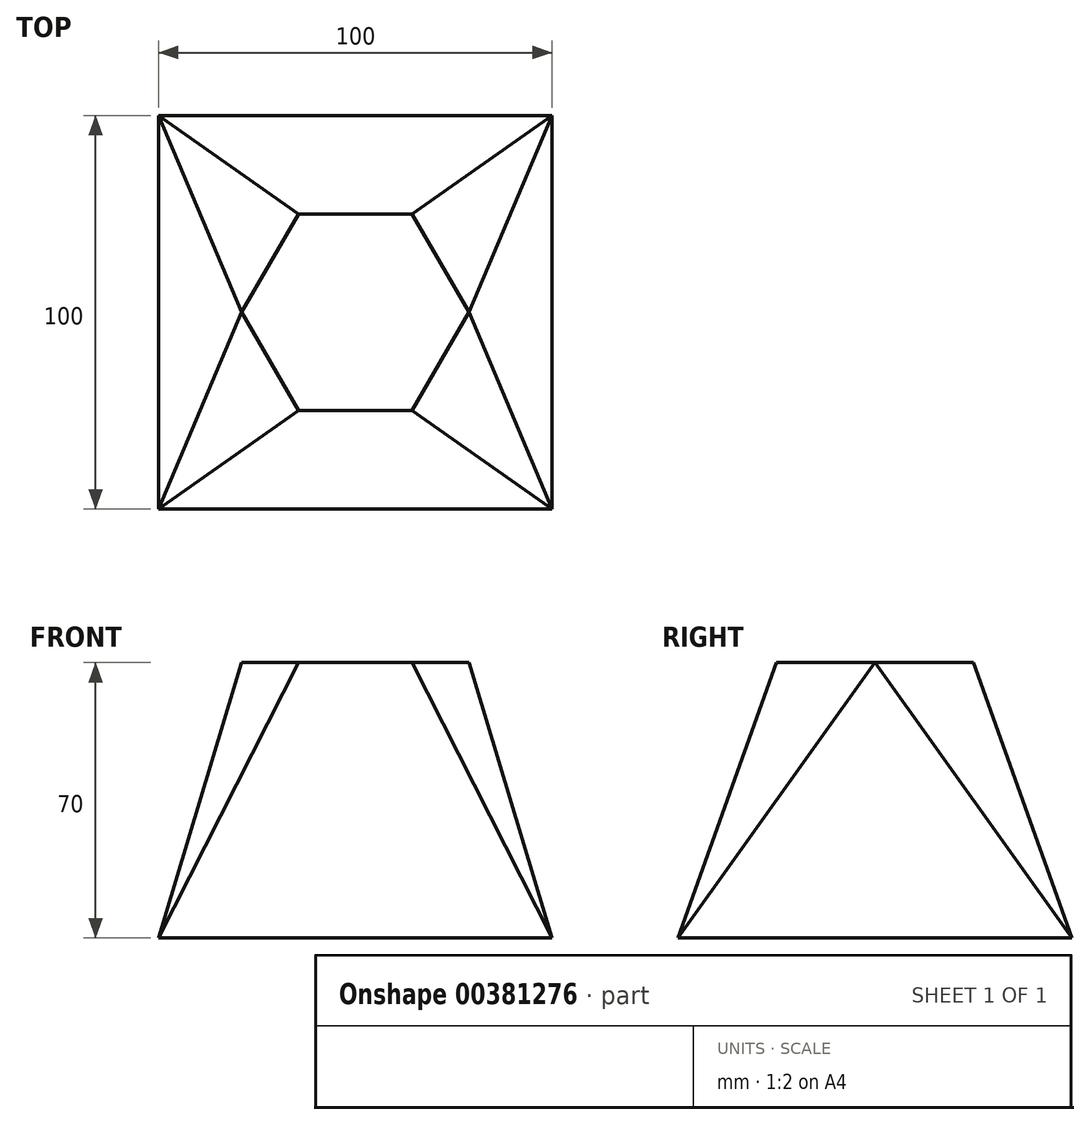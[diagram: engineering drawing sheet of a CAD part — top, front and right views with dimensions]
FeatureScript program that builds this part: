
annotation { "Feature Type Name" : "Feature", "Feature Type Description" : "" }
export const myFeature = defineFeature(function(context is Context, id is Id, definition is map)
    precondition{}
    {
        {
            var Q0;
            Q0=qCreatedBy(makeId("Top.planeOp"),FACE);
            var sketch = newSketch(context, id + "F0", { "sketchPlane" : qUnion([Q0])});
            skLineSegment(sketch, "E0.bottom", {"start": v(50, 50) * mm, "end": v(-50, 50) * mm});
            skLineSegment(sketch, "E0.top", {"start": v(50, -50) * mm, "end": v(-50, -50) * mm});
            skLineSegment(sketch, "E0.left", {"start": v(50, 50) * mm, "end": v(50, -50) * mm});
            skLineSegment(sketch, "E0.right", {"start": v(-50, 50) * mm, "end": v(-50, -50) * mm});
            skPoint(sketch, "E0.middle", {"position": v(0, 0) * mm});
            skSolve(sketch);
        }
        {
            var Q0;
            Q0=qCreatedBy(makeId("Top.planeOp"),FACE);
            cPlane(context, id + "F1", {"entities" : qUnion([Q0]), "cplaneType" : CPlaneType.OFFSET, "offset" : 70 * mm, "width" : 150 * mm, "height" : 150 * mm});
        }
        {
            var Q0;
            Q0=qCreatedBy(id+"F1.planeOp",FACE);
            var sketch = newSketch(context, id + "F2", { "sketchPlane" : qUnion([Q0])});
            skCircle(sketch, "E1.cCircle", {"center": v(0, 0) * mm, "radius": 25 * mm, "construction": true});
            skLineSegment(sketch, "E1.0", {"start": v(-14.43, 25) * mm, "end": v(14.43, 25) * mm});
            skLineSegment(sketch, "E1.1", {"start": v(14.43, 25) * mm, "end": v(28.87, 0) * mm});
            skLineSegment(sketch, "E1.2", {"start": v(28.87, 0) * mm, "end": v(14.43, -25) * mm});
            skLineSegment(sketch, "E1.3", {"start": v(14.43, -25) * mm, "end": v(-14.43, -25) * mm});
            skLineSegment(sketch, "E1.4", {"start": v(-14.43, -25) * mm, "end": v(-28.87, 0) * mm});
            skLineSegment(sketch, "E1.5", {"start": v(-28.87, 0) * mm, "end": v(-14.43, 25) * mm});
            skPoint(sketch, "E1.0.midPoint", {"position": v(0, 25) * mm});
            skSolve(sketch);
        }
        {
            var Q0;
            Q0=qCreatedBy(id+"F1.planeOp",FACE);
            var sketch = newSketch(context, id + "F3", { "sketchPlane" : qUnion([Q0])});
            skLineSegment(sketch, "E2.bottom", {"start": v(28.87, 25) * mm, "end": v(-28.87, 25) * mm});
            skLineSegment(sketch, "E2.top", {"start": v(28.87, -25) * mm, "end": v(-28.87, -25) * mm});
            skLineSegment(sketch, "E2.left", {"start": v(28.87, 25) * mm, "end": v(28.87, -25) * mm});
            skLineSegment(sketch, "E2.right", {"start": v(-28.87, 25) * mm, "end": v(-28.87, -25) * mm});
            skPoint(sketch, "E2.middle", {"position": v(0, 0) * mm});
            skSolve(sketch);
        }
        {
            var Q0;
            Q0=makeQuery(id+"F0.imprint","IMPRINT",FACE,{"disambiguationData":[TD([[makeQuery(id+"F0.imprint","IMPRINT",EDGE,{"derivedFrom":sQuery(id+"F0.wireOp",EDGE,"E0.bottom")}),1.0]])]});
            var Q1;
            Q1=makeQuery(id+"F3.imprint","IMPRINT",FACE,{"disambiguationData":[TD([[makeQuery(id+"F3.imprint","IMPRINT",EDGE,{"derivedFrom":sQuery(id+"F3.wireOp",EDGE,"E2.bottom")}),1.0]])]});
            loft(context, id + "F4", {"sheetProfilesArray" : [{ "sheetProfileEntities" : qUnion([Q0]) }, { "sheetProfileEntities" : qUnion([Q1]) }]});
        }
        {
            var Q0;
            Q0=makeQuery(id+"F4.opLoft","CAP_FACE",FACE,{"disambiguationData":[OSD([makeQuery(id+"F3.imprint","IMPRINT",FACE,{"disambiguationData":[TD([[makeQuery(id+"F3.imprint","IMPRINT",EDGE,{"derivedFrom":sQuery(id+"F3.wireOp",EDGE,"E2.bottom")}),1.0]])]})])],"isStart":true});
            var sketch = newSketch(context, id + "F5", { "sketchPlane" : qUnion([Q0])});
            skLineSegment(sketch, "E3", {"start": v(14.43, 25) * mm, "end": v(28.87, 0) * mm});
            skSolve(sketch);
        }
        {
            var Q1;
            {var subQ0=sQuery(id+"F5.wireOp",EDGE,"E3");Q1=makeQuery(id+"F5.imprint","IMPRINT",FACE,{"disambiguationData":[TD([[makeQuery(id+"F5.imprint","IMPRINT",EDGE,{"derivedFrom":subQ0}),1.0]])]});}
            var Q2;
            Q2=makeQuery(id+"F4.opLoft","MID_CAP_VERTEX",VERTEX,{"disambiguationData":[OSD([sQuery(id+"F0.wireOp",EDGE,"E0.bottom"),sQuery(id+"F0.wireOp",EDGE,"E0.left")])],"capPos":0.0});
            loft(context, id + "F6", {"sheetProfilesArray" : [{ "sheetProfileEntities" : qUnion([Q1]) }, { "sheetProfileEntities" : qUnion([Q2]) }]});
        }
        {
            var Q0;
            {var subQ0=sQuery(id+"F5.wireOp",EDGE,"E3");Q0=makeQuery(id+"F6.opLoft","SWEPT_BODY",BODY,{"disambiguationData":[OSD([sQuery(id+"F0.wireOp",EDGE,"E0.bottom"),sQuery(id+"F0.wireOp",EDGE,"E0.left"),makeQuery(id+"F5.imprint","IMPRINT",FACE,{"disambiguationData":[TD([[makeQuery(id+"F5.imprint","IMPRINT",EDGE,{"derivedFrom":subQ0}),1.0]])]})])]});}
            var Q1;
            Q1=qCreatedBy(makeId("Right.planeOp"),FACE);
            mirror(context, id + "F7", {"entities" : qUnion([Q0]), "mirrorPlane" : qUnion([Q1])});
        }
        {
            var Q0;
            {var subQ0=sQuery(id+"F5.wireOp",EDGE,"E3");Q0=makeQuery(id+"F7.opPattern","COPY",BODY,{"derivedFrom":makeQuery(id+"F6.opLoft","SWEPT_BODY",BODY,{"disambiguationData":[OSD([sQuery(id+"F0.wireOp",EDGE,"E0.bottom"),sQuery(id+"F0.wireOp",EDGE,"E0.left"),makeQuery(id+"F5.imprint","IMPRINT",FACE,{"disambiguationData":[TD([[makeQuery(id+"F5.imprint","IMPRINT",EDGE,{"derivedFrom":subQ0}),1.0]])]})])]}),"instanceName":"1"});}
            var Q1;
            Q1=makeQuery(id+"F4.opLoft","SWEPT_BODY",BODY,{"disambiguationData":[OSD([makeQuery(id+"F0.imprint","IMPRINT",FACE,{"disambiguationData":[TD([[makeQuery(id+"F0.imprint","IMPRINT",EDGE,{"derivedFrom":sQuery(id+"F0.wireOp",EDGE,"E0.bottom")}),1.0]])]}),makeQuery(id+"F3.imprint","IMPRINT",FACE,{"disambiguationData":[TD([[makeQuery(id+"F3.imprint","IMPRINT",EDGE,{"derivedFrom":sQuery(id+"F3.wireOp",EDGE,"E2.bottom")}),1.0]])]})])]});
            var Q2;
            Q2=qCreatedBy(makeId("Front.planeOp"),FACE);
            mirror(context, id + "F8", {"entities" : qUnion([Q0, Q1]), "mirrorPlane" : qUnion([Q2])});
        }
        {
            var Q0;
            {var subQ0=sQuery(id+"F5.wireOp",EDGE,"E3");Q0=makeQuery(id+"F6.opLoft","SWEPT_BODY",BODY,{"disambiguationData":[OSD([sQuery(id+"F0.wireOp",EDGE,"E0.bottom"),sQuery(id+"F0.wireOp",EDGE,"E0.left"),makeQuery(id+"F5.imprint","IMPRINT",FACE,{"disambiguationData":[TD([[makeQuery(id+"F5.imprint","IMPRINT",EDGE,{"derivedFrom":subQ0}),1.0]])]})])]});}
            var Q1;
            Q1=qCreatedBy(makeId("Front.planeOp"),FACE);
            mirror(context, id + "F9", {"entities" : qUnion([Q0]), "mirrorPlane" : qUnion([Q1])});
        }
        {
            var Q0;
            Q0=makeQuery(id+"F8.opPattern","COPY",BODY,{"derivedFrom":makeQuery(id+"F4.opLoft","SWEPT_BODY",BODY,{"disambiguationData":[OSD([makeQuery(id+"F0.imprint","IMPRINT",FACE,{"disambiguationData":[TD([[makeQuery(id+"F0.imprint","IMPRINT",EDGE,{"derivedFrom":sQuery(id+"F0.wireOp",EDGE,"E0.bottom")}),1.0]])]}),makeQuery(id+"F3.imprint","IMPRINT",FACE,{"disambiguationData":[TD([[makeQuery(id+"F3.imprint","IMPRINT",EDGE,{"derivedFrom":sQuery(id+"F3.wireOp",EDGE,"E2.bottom")}),1.0]])]})])]}),"instanceName":"1"});
            deleteBodies(context, id + "F10", {"entities" : qUnion([Q0])});
        }
        {
            var Q0;
            {var subQ0=sQuery(id+"F5.wireOp",EDGE,"E3");Q0=makeQuery(id+"F6.opLoft","SWEPT_BODY",BODY,{"disambiguationData":[OSD([sQuery(id+"F0.wireOp",EDGE,"E0.bottom"),sQuery(id+"F0.wireOp",EDGE,"E0.left"),makeQuery(id+"F5.imprint","IMPRINT",FACE,{"disambiguationData":[TD([[makeQuery(id+"F5.imprint","IMPRINT",EDGE,{"derivedFrom":subQ0}),1.0]])]})])]});}
            var Q1;
            {var subQ0=sQuery(id+"F5.wireOp",EDGE,"E3");Q1=makeQuery(id+"F7.opPattern","COPY",BODY,{"derivedFrom":makeQuery(id+"F6.opLoft","SWEPT_BODY",BODY,{"disambiguationData":[OSD([sQuery(id+"F0.wireOp",EDGE,"E0.bottom"),sQuery(id+"F0.wireOp",EDGE,"E0.left"),makeQuery(id+"F5.imprint","IMPRINT",FACE,{"disambiguationData":[TD([[makeQuery(id+"F5.imprint","IMPRINT",EDGE,{"derivedFrom":subQ0}),1.0]])]})])]}),"instanceName":"1"});}
            var Q2;
            {var subQ0=sQuery(id+"F5.wireOp",EDGE,"E3");Q2=makeQuery(id+"F8.opPattern","COPY",BODY,{"derivedFrom":makeQuery(id+"F7.opPattern","COPY",BODY,{"derivedFrom":makeQuery(id+"F6.opLoft","SWEPT_BODY",BODY,{"disambiguationData":[OSD([sQuery(id+"F0.wireOp",EDGE,"E0.bottom"),sQuery(id+"F0.wireOp",EDGE,"E0.left"),makeQuery(id+"F5.imprint","IMPRINT",FACE,{"disambiguationData":[TD([[makeQuery(id+"F5.imprint","IMPRINT",EDGE,{"derivedFrom":subQ0}),1.0]])]})])]}),"instanceName":"1"}),"instanceName":"1"});}
            var Q3;
            {var subQ0=sQuery(id+"F5.wireOp",EDGE,"E3");Q3=makeQuery(id+"F9.opPattern","COPY",BODY,{"derivedFrom":makeQuery(id+"F6.opLoft","SWEPT_BODY",BODY,{"disambiguationData":[OSD([sQuery(id+"F0.wireOp",EDGE,"E0.bottom"),sQuery(id+"F0.wireOp",EDGE,"E0.left"),makeQuery(id+"F5.imprint","IMPRINT",FACE,{"disambiguationData":[TD([[makeQuery(id+"F5.imprint","IMPRINT",EDGE,{"derivedFrom":subQ0}),1.0]])]})])]}),"instanceName":"1"});}
            var Q4;
            Q4=makeQuery(id+"F4.opLoft","SWEPT_BODY",BODY,{"disambiguationData":[OSD([makeQuery(id+"F0.imprint","IMPRINT",FACE,{"disambiguationData":[TD([[makeQuery(id+"F0.imprint","IMPRINT",EDGE,{"derivedFrom":sQuery(id+"F0.wireOp",EDGE,"E0.bottom")}),1.0]])]}),makeQuery(id+"F3.imprint","IMPRINT",FACE,{"disambiguationData":[TD([[makeQuery(id+"F3.imprint","IMPRINT",EDGE,{"derivedFrom":sQuery(id+"F3.wireOp",EDGE,"E2.bottom")}),1.0]])]})])]});
            booleanBodies(context, id + "F11", {"operationType" : BooleanOperationType.SUBTRACTION, "tools" : qUnion([Q0, Q1, Q2, Q3]), "targets" : qUnion([Q4])});
        }
    });
